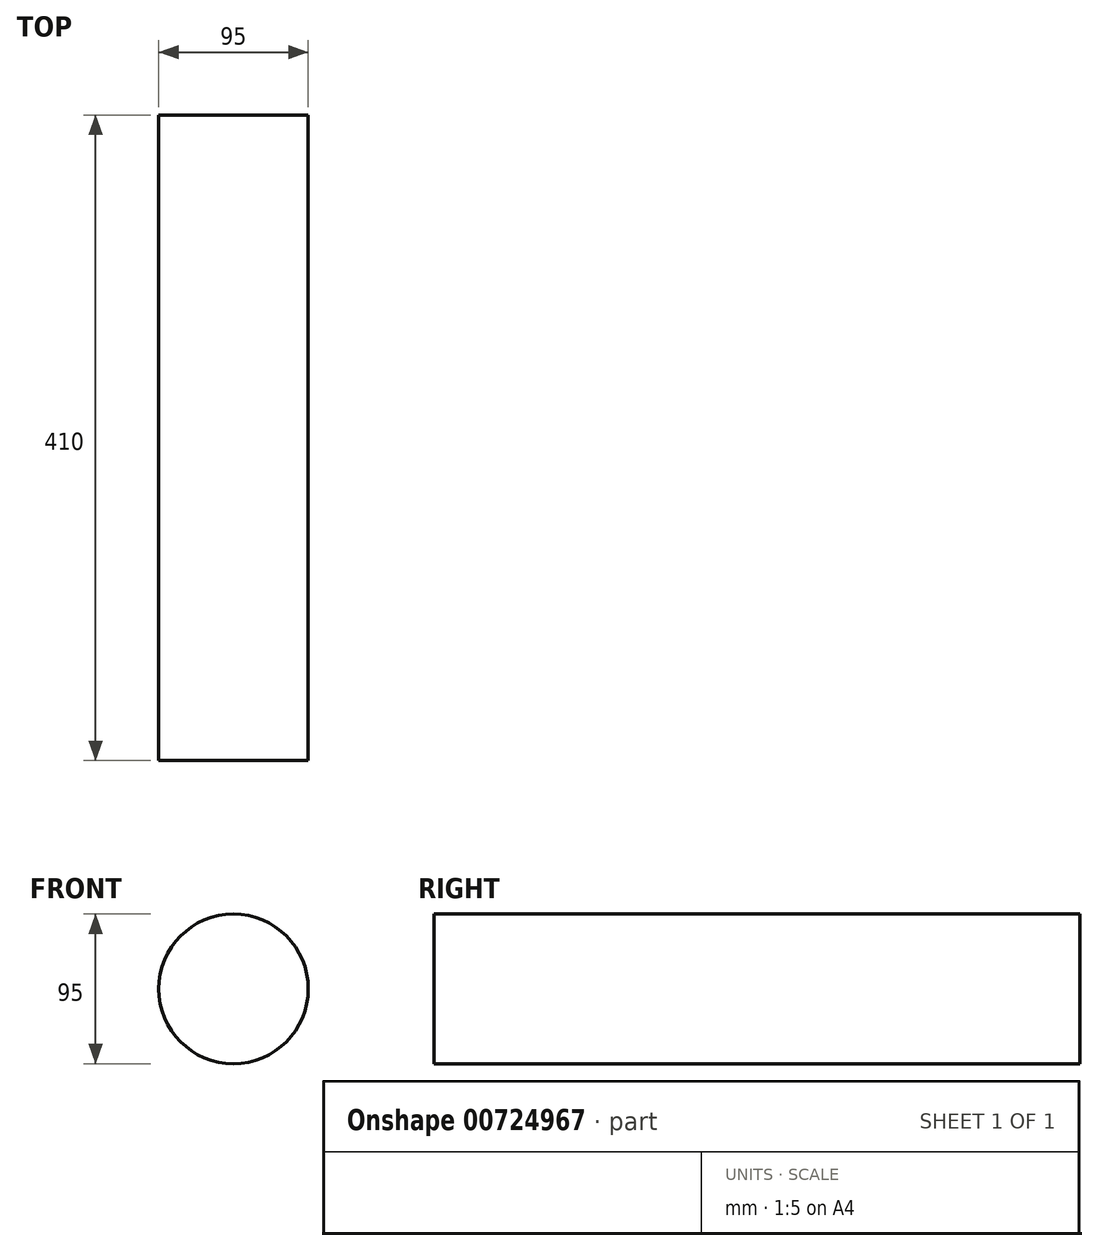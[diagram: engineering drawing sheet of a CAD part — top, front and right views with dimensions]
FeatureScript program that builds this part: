
annotation { "Feature Type Name" : "Feature", "Feature Type Description" : "" }
export const myFeature = defineFeature(function(context is Context, id is Id, definition is map)
    precondition{}
    {
        {
            var Q0;
            Q0=qCreatedBy(makeId("Front.planeOp"),FACE);
            var sketch = newSketch(context, id + "F0", { "sketchPlane" : qUnion([Q0])});
            skCircle(sketch, "E0", {"center": v(0, 0) * mm, "radius": 47.5 * mm});
            skCircle(sketch, "E1.0", {"center": v(0, 0) * mm, "radius": 47.2 * mm});
            skSolve(sketch);
        }
        {
            var Q0;
            Q0=makeQuery(id+"F0.imprint","IMPRINT",FACE,{"disambiguationData":[TD([[makeQuery(id+"F0.imprint","IMPRINT",EDGE,{"derivedFrom":sQuery(id+"F0.wireOp",EDGE,"E0")}),1.0]])]});
            var Q1;
            Q1=sQuery(id+"F0.wireOp",EDGE,"E0");
            extrude(context, id + "F1", {"entities" : qUnion([Q0]), "bodyType" : ToolBodyType.SURFACE, "surfaceEntities" : qUnion([Q1]), "depth" : 410 * mm, "offsetDistance" : 25 * mm, "symmetric" : true});
        }
    });
